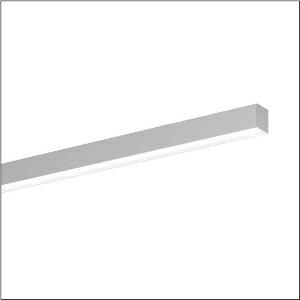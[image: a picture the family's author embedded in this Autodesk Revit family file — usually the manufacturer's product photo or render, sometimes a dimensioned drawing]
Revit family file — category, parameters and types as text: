
# Revit family: silica_21_51mx20db32sb
name_source: partatom
category: Lighting Fixtures
units: mm (PartAtom-declared; Revit-internal decimal feet)

## family parameters
Cut with Voids When Loaded = No
Host = Face
Light Source = No
Part Type = Normal
Room Calculation Point = No
Round Connector Dimension = Use Diameter
Shared = No

## types (1)
- --- (1 x LED, 3000 lm, 20.2 W, 3000K)
    Apparent Load = 20 VA
    CIE Flux Codes = 48 79 96 100 100
    Color Rendering = 80
    Color Temperature = 3000K
    Default Elevation = 1800 mm
    Description = Silica 21, office luminaire, primary optical cover: cover, of PMMA, opal, light emission: direct distribution, primary light characteristic: symmetric, installation type: surface-mounted, LED, rated luminous flux: 3.000lm, luminous efficacy: 149lm/W, light colour: 830, colour temperature: 3000K, control gear: DALI 2, with terminal, 3+2-pole, max. 2.5mm², mains connection: 220..240V, AC, 50/60Hz, luminaire housing, of aluminium, metallic grey (RAL 9006), length: 1.504mm, width: 53mm, height: 53mm, protection rating (complete): IP20, insulation class (complete): insulation class I (protective earthing), certification: CE, permissible operating ambient temperature: 0..+35°C, standard: EN 50419, packaging unit: 1 piece
    Height = 53 mm
    Lamp = 1 x LED
    Lamp Light Flux = 3000 lm
    Lamp Power = 20.2 W
    Lamp count = 1
    Length = 1504 mm
    Luminous efficacy = 149 lm/W
    Manufacturer = Siteco
    ModVariant = No
    Model = 51MX20DB32SB
    Mounting Place = Ceiling
    Mounting Type = Surface mounted
    Number of Poles = 1
    OnlyDefault = Yes
    Power Factor = 1
    Product Name = Silica 21
    Product group = office luminaire | ceiling mounted
    ProductGroupID = 301
    Protection Class = Protection class I
    Protection Degree = IP 20
    RLX_Detail_Level = 1
    RLX_Emergency_Light_Flux = 0 lm
    RLX_Emergency_Type = 0
    RLX_Emergency_Type_DB = No
    RlxData = <blob elided: 26053 chars, md5=49865440>
    Socket = socket
    Standby Power = 0 W
    System Light Flux = 3000 lm
    System Power = 20 W
    Type Comments = factory setting: luminous flux: 100 % | dim-lin: 254 | 233 mA
    Type Image = l_1335933.jpg
    URL = http://relux.com
    VarID = @adj_119693
    Voltage = 0 V
    Weight = 0.00 kg
    Width = 53 mm

## geometry (parser evidence)
native form markers: Blend x4, Sweep x11
no freeform markers — native parametric forms only
